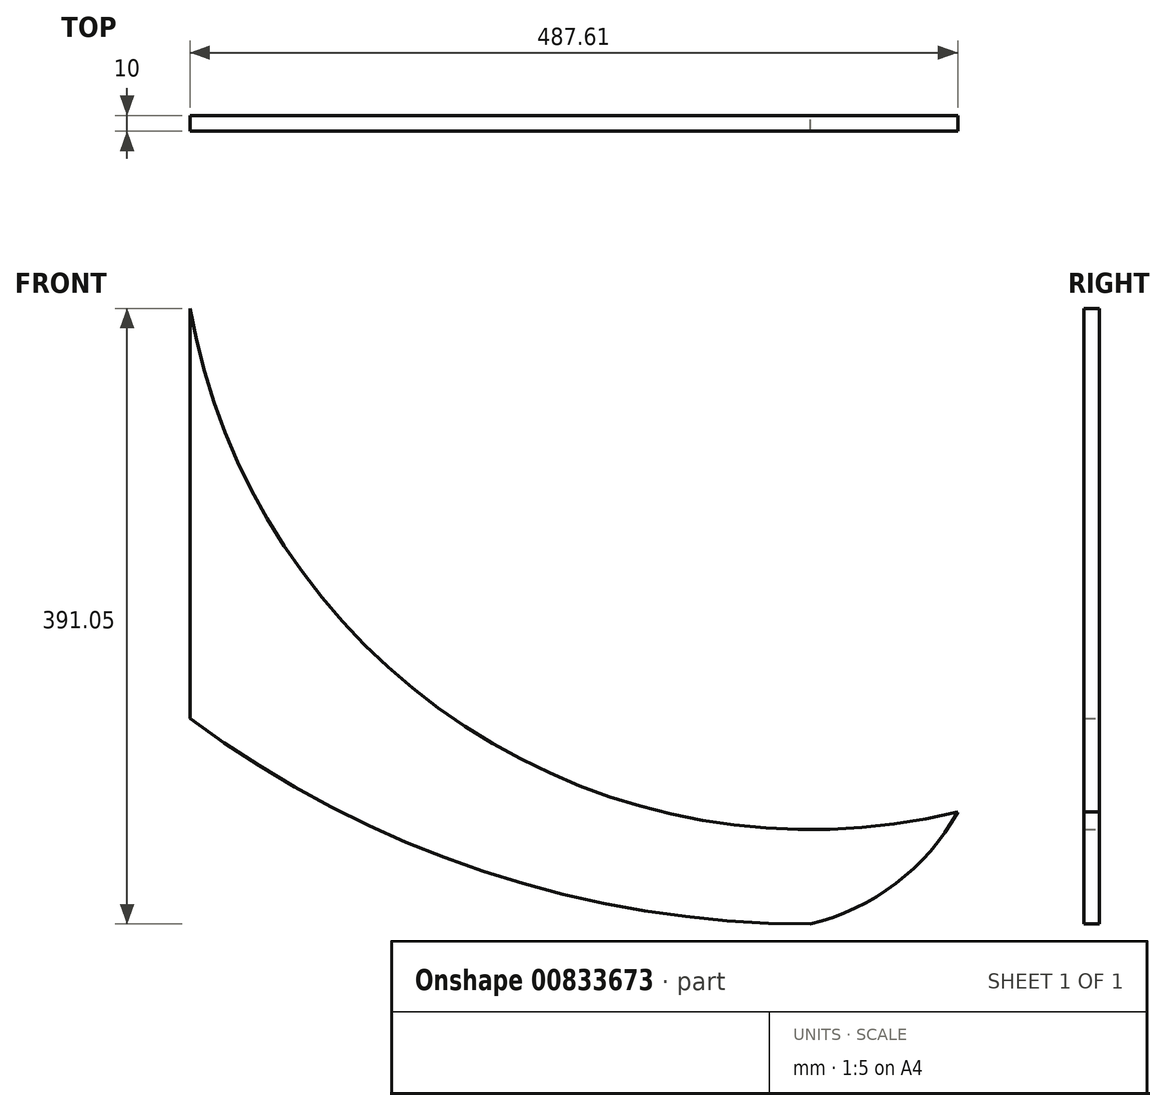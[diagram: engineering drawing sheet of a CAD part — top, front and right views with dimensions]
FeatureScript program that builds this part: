
annotation { "Feature Type Name" : "Feature", "Feature Type Description" : "" }
export const myFeature = defineFeature(function(context is Context, id is Id, definition is map)
    precondition{}
    {
        {
            var Q0;
            Q0=qCreatedBy(makeId("Front.planeOp"),FACE);
            var sketch = newSketch(context, id + "F0", { "sketchPlane" : qUnion([Q0])});
            skLineSegment(sketch, "E0", {"start": v(0, 0) * mm, "end": v(500, 0) * mm});
            skLineSegment(sketch, "E1", {"start": v(0, 396.98) * mm, "end": v(0, -385.65) * mm});
            skSolve(sketch);
        }
        {
            var Q0;
            Q0=qCreatedBy(makeId("Front.planeOp"),FACE);
            var sketch = newSketch(context, id + "F1", { "sketchPlane" : qUnion([Q0])});
            skPoint(sketch, "E2", {"position": v(400, 300) * mm});
            skArc(sketch, "E3", {"start": v(0, 300) * mm, "mid": v(117.16, 17.16) * mm, "end": v(400, -100) * mm});
            skPoint(sketch, "E4", {"position": v(400, 0) * mm});
            skArc(sketch, "E5", {"start": v(400, -100) * mm, "mid": v(470.71, -70.71) * mm, "end": v(500, 0) * mm});
            skSolve(sketch);
        }
        {
            var Q0;
            Q0=qCreatedBy(makeId("Front.planeOp"),FACE);
            var sketch = newSketch(context, id + "F2", { "sketchPlane" : qUnion([Q0])});
            skPoint(sketch, "E6", {"position": v(400, 500) * mm});
            skArc(sketch, "E7", {"start": v(0, -24.98) * mm, "mid": v(188.91, -125.33) * mm, "end": v(400, -160) * mm});
            skPoint(sketch, "E8", {"position": v(400, -50) * mm});
            skPoint(sketch, "E9", {"position": v(120, 0) * mm});
            skLineSegment(sketch, "E10", {"start": v(500.99, 0) * mm, "end": v(510.99, 0) * mm});
            skPoint(sketch, "E11", {"position": v(400, -160) * mm});
            skPoint(sketch, "E12", {"position": v(489.32, -96.1) * mm});
            skPoint(sketch, "E13", {"position": v(510.99, 0) * mm});
            skArc(sketch, "E14", {"start": v(400, -160) * mm, "mid": v(476.16, -113.75) * mm, "end": v(511.38, -31.9) * mm});
            skPoint(sketch, "E15", {"position": v(0, -24.98) * mm});
            skPoint(sketch, "E16", {"position": v(5.99, 22.61) * mm});
            skLineSegment(sketch, "E17", {"start": v(5.99, 22.61) * mm, "end": v(5.99, 231.05) * mm});
            skLineSegment(sketch, "E18", {"start": v(5.99, 664.97) * mm, "end": v(5.99, 368.95) * mm});
            skLineSegment(sketch, "E19", {"start": v(510.99, 0) * mm, "end": v(500.99, 0) * mm});
            skLineSegment(sketch, "E20", {"start": v(510.99, 0) * mm, "end": v(511.38, -31.9) * mm});
            skLineSegment(sketch, "E21", {"start": v(500.99, 0) * mm, "end": v(501.04, -4.2) * mm});
            skPoint(sketch, "E22", {"position": v(501.04, -4.2) * mm});
            skPoint(sketch, "E23", {"position": v(400, 0) * mm});
            skArc(sketch, "E24", {"start": v(400, -100) * mm, "mid": v(440.84, -91.28) * mm, "end": v(474.56, -66.64) * mm});
            skPoint(sketch, "E25", {"position": v(474.56, -66.64) * mm});
            skPoint(sketch, "E26", {"position": v(400, -100) * mm});
            skArc(sketch, "E27", {"start": v(400, -100) * mm, "mid": v(469.35, -71.95) * mm, "end": v(501.04, -4.2) * mm});
            skPoint(sketch, "E28", {"position": v(400, 300) * mm});
            skArc(sketch, "E29", {"start": v(5.99, 231.05) * mm, "mid": v(180.56, -34.43) * mm, "end": v(493.6, -88.9) * mm});
            skLineSegment(sketch, "E30.trimOffspring", {"start": v(5.99, 231.05) * mm, "end": v(5.99, -29.48) * mm});
            skLineSegment(sketch, "E31.trimOffspring", {"start": v(5.99, 368.95) * mm, "end": v(5.99, 664.97) * mm});
            skSolve(sketch);
        }
        {
            var Q0;
            Q0=makeQuery(id+"F2.imprint","IMPRINT",FACE,{"disambiguationData":[TD([[makeQuery(id+"F2.imprint","IMPRINT",EDGE,{"derivedFrom":sQuery(id+"F2.wireOp",EDGE,"E19")}),1.0]])]});
            var Q1;
            {var subQ4=sQuery(id+"F2.wireOp",EDGE,"E14");var subQ5=sQuery(id+"F2.wireOp",EDGE,"E7");var subQ6=makeQuery(id+"F2.imprint","INTERSECT",VERTEX,{"derivedFrom":[subQ5,subQ4]});Q1=makeQuery(id+"F2.imprint","IMPRINT",FACE,{"disambiguationData":[TD([[makeQuery(id+"F2.imprint","IMPRINT",EDGE,{"disambiguationData":[TD([[subQ6,1.0]])],"derivedFrom":subQ5}),1.0]])]});}
            extrude(context, id + "F3", {"entities" : qUnion([Q0, Q1]), "depth" : 10 * mm, "offsetDistance" : 25 * mm});
        }
    });
